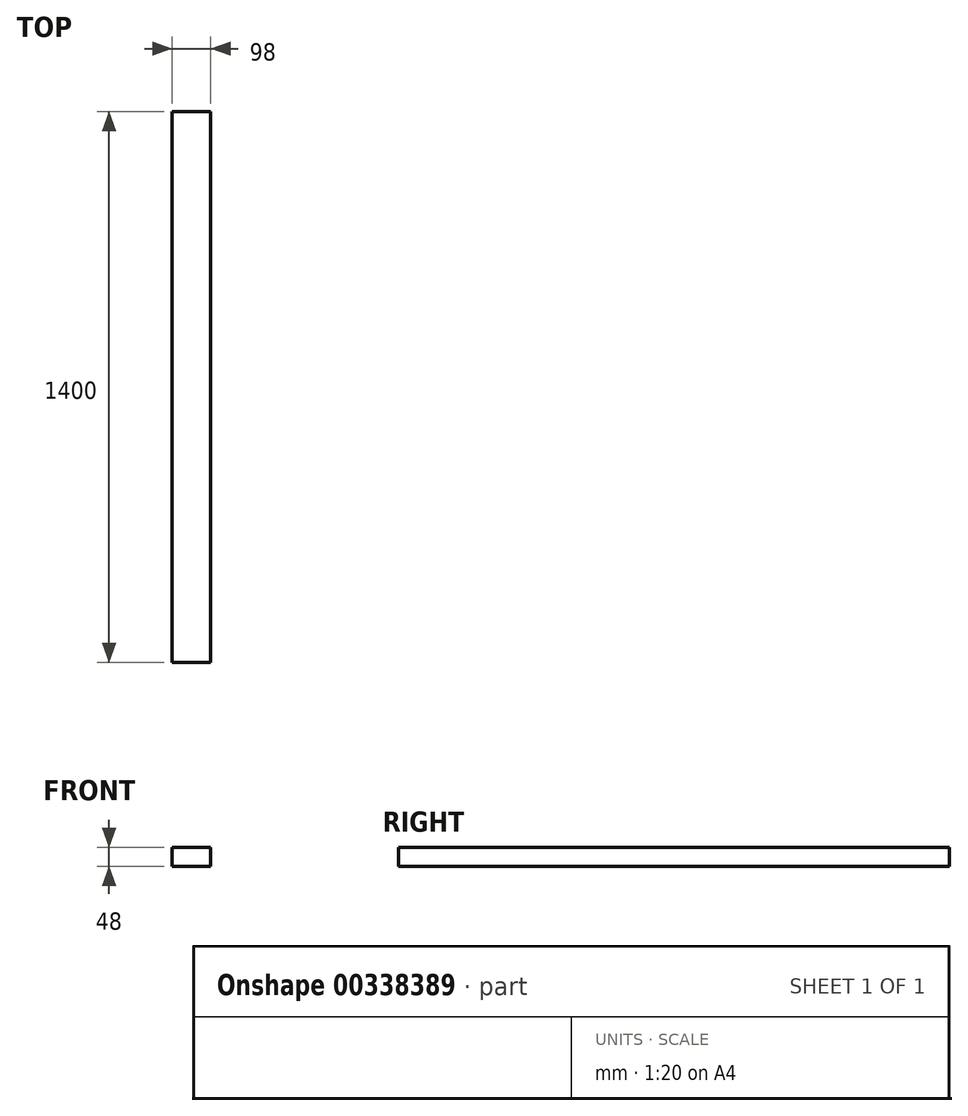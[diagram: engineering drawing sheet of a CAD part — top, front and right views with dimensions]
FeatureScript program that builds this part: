
annotation { "Feature Type Name" : "Feature", "Feature Type Description" : "" }
export const myFeature = defineFeature(function(context is Context, id is Id, definition is map)
    precondition{}
    {
        {
            var Q0;
            Q0=qCreatedBy(makeId("Front.planeOp"),FACE);
            var sketch = newSketch(context, id + "F0", { "sketchPlane" : qUnion([Q0])});
            skLineSegment(sketch, "E0.bottom", {"start": v(-49, -24) * mm, "end": v(49, -24) * mm});
            skLineSegment(sketch, "E0.top", {"start": v(-49, 24) * mm, "end": v(49, 24) * mm});
            skLineSegment(sketch, "E0.left", {"start": v(-49, -24) * mm, "end": v(-49, 24) * mm});
            skLineSegment(sketch, "E0.right", {"start": v(49, -24) * mm, "end": v(49, 24) * mm});
            skPoint(sketch, "E0.middle", {"position": v(0, 0) * mm});
            skSolve(sketch);
        }
        {
            var Q0;
            Q0=makeQuery(id+"F0.imprint","IMPRINT",FACE,{"disambiguationData":[TD([[makeQuery(id+"F0.imprint","IMPRINT",EDGE,{"derivedFrom":sQuery(id+"F0.wireOp",EDGE,"E0.bottom")}),1.0]])]});
            extrude(context, id + "F1", {"entities" : qUnion([Q0]), "depth" : 1400 * mm});
        }
    });
